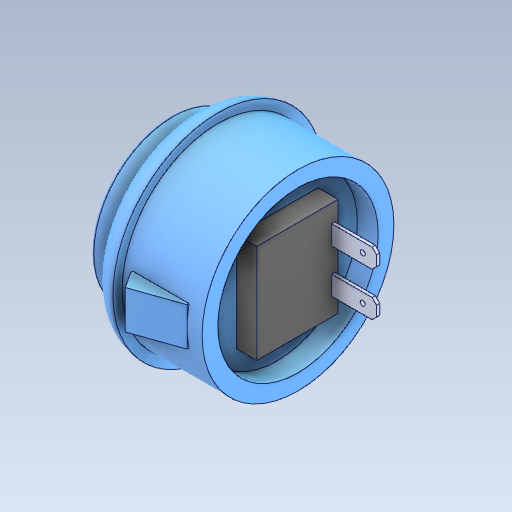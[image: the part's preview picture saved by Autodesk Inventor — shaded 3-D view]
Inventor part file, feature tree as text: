
AUTODESK INVENTOR PART (.ipt)
format: ipt  version: 2020 (Build 240168000, 168)  size: 223,232 bytes
history: mixed  units: mm
features: fillet x1, imported_body x1
ambient origin geometry x8: Origin, YZ Plane, XZ Plane, XY Plane, X Axis, Y Axis, Z Axis, Center Point
bodies: Solid1 (imported_parasolid)
feature tree (2):
  fillet  "Fillet1"  [1 undecoded]
  imported_body  NMx_Import_Brep_tag  [imported B-rep: ~46 faces, bbox_mm=[26.9, 28.725, 34.9]]
note: 1 required parameter value undecoded (feature->parameter linkage not recoverable at this tier; creation-order binding heuristic only, values carry confidence <= 0.55)
